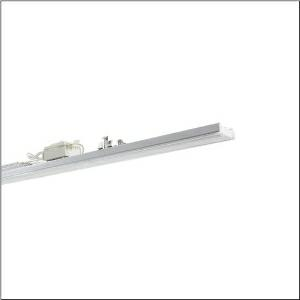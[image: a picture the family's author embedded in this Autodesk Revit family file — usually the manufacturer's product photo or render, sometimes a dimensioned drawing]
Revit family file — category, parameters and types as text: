
# Revit family: licross_11_recessed_ho_51te1edv4lxs
name_source: partatom
category: Lighting Fixtures
units: mm (PartAtom-declared; Revit-internal decimal feet)

## family parameters
Cut with Voids When Loaded = No
Host = Face
Light Source = No
Part Type = Normal
Room Calculation Point = No
Round Connector Dimension = Use Diameter
Shared = No

## types (1)
- --- (1 x LED, 20440 lm, 111.8 W, 4000K)
    Apparent Load = 112 VA
    CIE Flux Codes = 85 95 99 100 100
    Color Rendering = 80
    Color Temperature = 4000K
    Default Elevation = 1800 mm
    Description = Licross 11 Recessed HO, luminaire insert, of sheet steel, galvanised, coil coated, white, length: 2.250mm, width: 66mm, height: 67mm, LED rated luminous flux: 20.440lm, light colour: 840, SDCM (Standard Deviation of Colour Matching)MacAdam ≤ 2 SDCM (initial), control gear: DALI 2, with plug, 5-pole, with phase selection, mains connection: 220..240V, AC, 50/60Hz, rated input power: 112W, internal wiring halogen-free, primary light control with lens, of plastic, primary optical cover: cover, of PMMA, light emission: direct distribution, primary light characteristic: symmetric, protection rating (complete): IP54, insulation class (complete): insulation class I (protective earthing), certification: CE, ENEC, VDE, UKCA, protection symbol: D if used in an environment with non-conductive dust loads with corresponding accessories, impact resistance: IK06, permissible ambient temperature for indoor applications: -40..+45°C, corresponds to IFS (International Featured Standards) requirements for safety and quality in the food industry, reducing of maximum allowable ambient temperature of 5°C with ceiling mounting, LABS conformity tested according to VDMA 24364:2018-05, The light source and the operating device comply with the requirements of the Ecodesign Regulation (EU) 2019/2020 and are replaceable in accordance with this regulation, packaging unit: 1 piece
    Height = 58 mm
    Lamp = 1 x LED
    Lamp Light Flux = 20440 lm
    Lamp Power = 111.8 W
    Lamp count = 1
    Length = 2250 mm
    Luminous efficacy = 183 lm/W
    Manufacturer = Siteco
    ModVariant = No
    Model = 51TE1EDV4LXS
    Mounting Place = Ceiling
    Mounting Type = Pendant
    Number of Poles = 1
    OnlyDefault = Yes
    Power Factor = 1
    Product Name = Licross 11 Recessed HO
    Product group = luminaire insert | ceiling pendant
    ProductGroupID = 901
    Protection Class = Protection class I
    Protection Degree = IP 54
    RLX_Detail_Level = 1
    RLX_Emergency_Light_Flux = 0 lm
    RLX_Emergency_Type = 0
    RLX_Emergency_Type_DB = No
    RlxData = <blob elided: 30037 chars, md5=f935d442>
    Socket = socket
    Standby Power = 0 W
    System Light Flux = 20440 lm
    System Power = 112 W
    Type Comments = factory setting: luminous flux: 100 % | dim-lin: 254 | 520 mA
    Type Image = l_1296930.jpg
    URL = http://relux.com
    VarID = @adj_099561
    Voltage = 0 V
    Weight = 0.00 kg
    Width = 66 mm

## geometry (parser evidence)
native form markers: Blend x4, Sweep x12
no freeform markers — native parametric forms only
